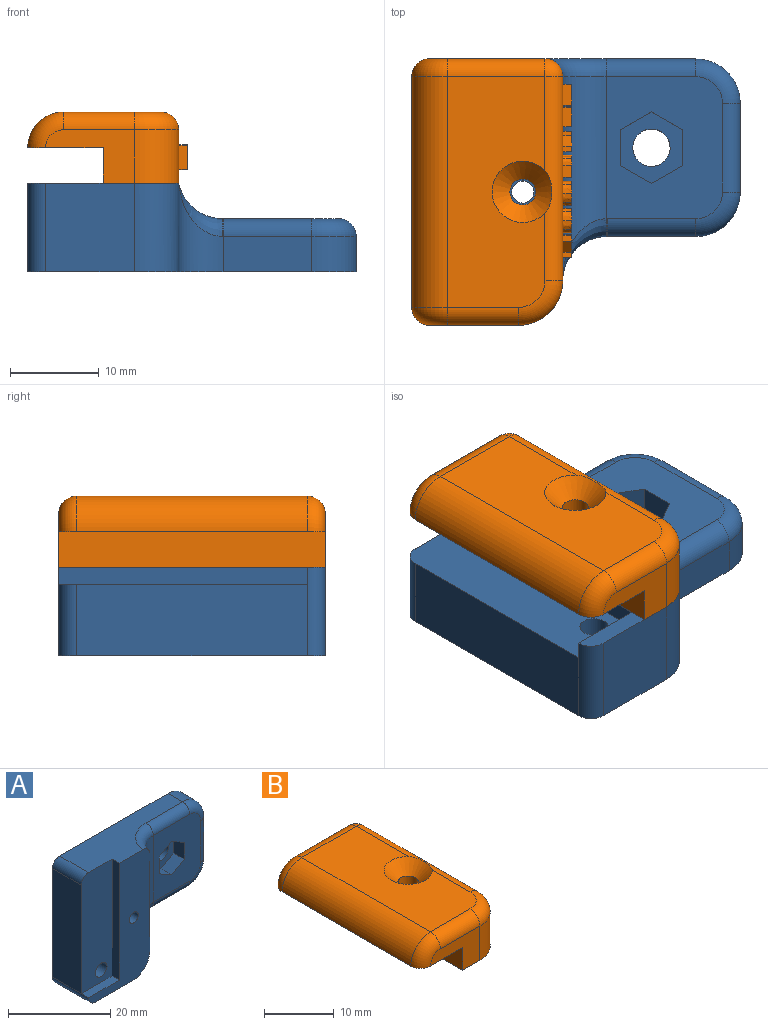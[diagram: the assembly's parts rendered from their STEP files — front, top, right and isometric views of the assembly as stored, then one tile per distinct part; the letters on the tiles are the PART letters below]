
ASSEMBLY  parts=2 mates=1
PART A: 43 faces, bbox 37.6x10.4x30.6 mm
  f0: cylinder r=1.6mm len=5.5mm, axis (0,-1,0), area 55.3mm2, adj f9,f32
  f1: cylinder r=2.1mm len=4.2mm, axis (0,-1,0), area 39.6mm2, adj f4,f25
  f2: plane 30x10mm, normal (0,0,1), area 194.9mm2, adj f3,f4,f8,f9,f18,f33,f34,f42
  f3: plane 30.15x17.15mm, normal (0,-1,0), area 260mm2, adj f2,f6,f7,f8,f13,f14,f15,f33
  f4: plane 37x30mm, normal (0,1,0), area 847.6mm2, adj f1,f2,f5,f6,f11,f12,f13,f14
  f5: plane 26x8mm, normal (-1,0,0), area 208mm2, adj f4,f9,f41,f42
  f6: plane 10x10mm, normal (0,0,-1), area 100mm2, adj f3,f4,f14,f41
  f7: plane 8.5x2mm, normal (0,0,1), area 17mm2, adj f3,f8,f9,f41
  f8: plane 28x2mm, normal (-1,0,0), area 56mm2, adj f2,f3,f7,f9
  f9: plane 28x8.5mm, normal (0,-1,0), area 229.1mm2, adj f0,f2,f5,f7,f8,f42
  f10: plane 16x13.1mm, normal (0,-1,0), area 163.3mm2, adj f15,f19,f20,f21,f22,f23,f24,f34
  f11: plane 10x4mm, normal (0,0,-1), area 40mm2, adj f4,f16,f17,f38
  f12: plane 10x4mm, normal (1,0,0), area 40mm2, adj f4,f17,f18,f36
  f13: cylinder r=1.25mm len=10mm, axis (0,-1,0), area 78.5mm2, adj f3,f4
  f14: cylinder r=5mm len=10mm, axis (0,1,0), area 78.5mm2, adj f3,f4,f6,f16,f40
  f15: cylinder r=5mm len=22.25mm, axis (0,0,1), area 124.1mm2, adj f3,f10,f33,f40
  f16: cylinder r=5mm len=9.82mm, axis (0,-1,0), area 49.9mm2, adj f4,f11,f14,f39,f40
  f17: cylinder r=5mm len=5mm, axis (0,-1,0), area 31.4mm2, adj f4,f11,f12,f37
  f18: cylinder r=5mm len=5mm, axis (0,1,0), area 31.4mm2, adj f2,f4,f12,f35
  f19: plane 3.5x3mm, normal (0.5,0,0.87), area 12.1mm2, adj f10,f20,f24,f25
  f20: plane 3.5x3mm, normal (-0.5,0,0.87), area 12.1mm2, adj f10,f19,f21,f25
  f21: plane 4.04x3mm, normal (-1,0,0), area 12.1mm2, adj f10,f20,f22,f25
  f22: plane 3.5x3mm, normal (-0.5,0,-0.87), area 12.1mm2, adj f10,f21,f23,f25
  f23: plane 3.5x3mm, normal (0.5,0,-0.87), area 12.1mm2, adj f10,f22,f24,f25
  f24: plane 4.04x3mm, normal (1,0,0), area 12.1mm2, adj f10,f19,f23,f25
  f25: plane 8.08x7mm, normal (0,-1,0), area 28.6mm2, adj f1,f19,f20,f21,f22,f23,f24
  f26: plane 3.46x2.5mm, normal (0,0,1), area 8.7mm2, adj f4,f27,f31,f32
  f27: plane 3x2.5mm, normal (0.87,0,0.5), area 8.7mm2, adj f4,f26,f28,f32
  f28: plane 3x2.5mm, normal (0.87,0,-0.5), area 8.7mm2, adj f4,f27,f29,f32
  f29: plane 3.46x2.5mm, normal (0,0,-1), area 8.7mm2, adj f4,f28,f30,f32
  f30: plane 3x2.5mm, normal (-0.87,0,-0.5), area 8.7mm2, adj f4,f29,f31,f32
  f31: plane 3x2.5mm, normal (-0.87,0,0.5), area 8.7mm2, adj f4,f26,f30,f32
  f32: plane 6.93x6mm, normal (0,1,0), area 23.1mm2, adj f0,f26,f27,f28,f29,f30,f31
  f33: torus R=7mm, axis (0,0,1), area 25.2mm2, adj f2,f3,f15,f34
  f34: cylinder r=2mm len=10.1mm, axis (-1,0,0), area 31.7mm2, adj f2,f10,f33,f35
  f35: torus R=3mm, axis (0,-1,0), area 21.1mm2, adj f10,f18,f34,f36
  f36: cylinder r=2mm len=10mm, axis (0,0,1), area 31.4mm2, adj f10,f12,f35,f37
  f37: torus R=3mm, axis (0,-1,0), area 21.1mm2, adj f10,f17,f36,f38
  f38: cylinder r=2mm len=10mm, axis (1,0,0), area 31.4mm2, adj f10,f11,f37,f39
  f39: torus R=7mm, axis (0,-1,0), area 0.3mm2, adj f10,f16,f38,f40
  f40: bspline ~7.5x6.16mm, area 17.8mm2, adj f3,f14,f15,f16,f39
  f41: cylinder r=2mm len=10mm, axis (0,-1,0), area 31.4mm2, adj f3,f4,f5,f6,f7
  f42: cylinder r=2mm len=8mm, axis (0,1,0), area 25.1mm2, adj f2,f4,f5,f9
PART B: 125 faces, bbox 18.3x30.4x8.3 mm
  f0: plane 23.02x6mm, normal (1,0,0), area 107.4mm2, adj f1,f9,f12,f14,f19,f20,f21,f22
  f1: plane 30.02x8.5mm, normal (0,0,-1), area 242.4mm2, adj f0,f2,f3,f4,f7,f9,f12
  f2: plane 13x6mm, normal (0,1,0), area 51.1mm2, adj f1,f6,f7,f10,f11,f12
  f3: plane 10x6mm, normal (0,-1,0), area 33.1mm2, adj f1,f6,f7,f9,f16,f17
  f4: cylinder r=1.45mm len=6mm, axis (0,0,-1), area 54.7mm2, adj f1,f18
  f5: plane 26.02x11mm, normal (0,0,1), area 250mm2, adj f8,f11,f14,f15,f16,f18
  f6: plane 30.02x8.5mm, normal (0,0,-1), area 253.5mm2, adj f2,f3,f7,f8,f10,f17
  f7: plane 30.02x4mm, normal (-1,0,0), area 120.1mm2, adj f1,f2,f3,f6
  f8: cylinder r=4mm len=26.02mm, axis (0,1,0), area 163.5mm2, adj f5,f6,f10,f17
  f9: cylinder r=5mm len=6mm, axis (0,0,1), area 47.1mm2, adj f0,f1,f3,f15
  f10: torus R=2mm, axis (0,1,0), area 16.2mm2, adj f2,f6,f8,f11
  f11: cylinder r=2mm len=11mm, axis (1,0,0), area 34.6mm2, adj f2,f5,f10,f13
  f12: cylinder r=2mm len=6mm, axis (0,0,-1), area 18.8mm2, adj f0,f1,f2,f13
  f13: sphere r=2mm, area 6.3mm2, adj f11,f12,f14
  f14: cylinder r=2mm len=23.02mm, axis (0,-1,0), area 69.6mm2, adj f0,f5,f13,f15,f18
  f15: torus R=3mm, axis (0,0,1), area 21.1mm2, adj f5,f9,f14,f16
  f16: cylinder r=2mm len=8mm, axis (-1,0,0), area 25.1mm2, adj f3,f5,f15,f17
  f17: torus R=2mm, axis (0,1,0), area 16.2mm2, adj f3,f6,f8,f16
  f18: cone r=1.45mm half-angle=45deg, axis (0,0,1), area 43mm2, adj f4,f5,f14
  f19: plane 1.25x1mm, normal (0,-0.79,-0.62), area 1.6mm2, adj f0,f20,f30,f31
  f20: plane 1x0.67mm, normal (0,0,-1), area 0.7mm2, adj f0,f19,f21,f31
  f21: plane 1.57x1.26mm, normal (0,0.78,0.63), area 2mm2, adj f0,f20,f22,f31
  f22: plane 1.16x1.15mm, normal (0,0.7,-0.71), area 1.6mm2, adj f0,f21,f23,f31
  f23: plane 1x0.66mm, normal (0,0,1), area 0.7mm2, adj f0,f22,f24,f31
  f24: plane 1.23x1.23mm, normal (0,-0.71,0.7), area 1.7mm2, adj f0,f23,f25,f31
  f25: plane 1.23x1mm, normal (0,1,0), area 1.2mm2, adj f0,f24,f26,f31
  f26: plane 1x0.57mm, normal (0,0,1), area 0.6mm2, adj f0,f25,f27,f31
  f27: plane 2.72x1mm, normal (0,-1,0), area 2.7mm2, adj f0,f26,f28,f31
  f28: plane 1x0.57mm, normal (0,0,-1), area 0.6mm2, adj f0,f27,f29,f31
  f29: plane 1x0.99mm, normal (0,1,0), area 1mm2, adj f0,f28,f30,f31
  f30: plane 1x0.34mm, normal (0,0.61,-0.79), area 0.4mm2, adj f0,f19,f29,f31
  f31: plane 2.72x2.55mm, normal (1,0,0), area 3.4mm2, adj f19,f20,f21,f22,f23,f24,f25,f26
  f32: extruded ~1x0.69mm, area 0.7mm2, adj f33,f48,f49,f50
  f33: extruded ~1x0.71mm, area 0.8mm2, adj f32,f34,f49,f50
  f34: extruded ~1x0.59mm, area 0.7mm2, adj f33,f35,f49,f50
  f35: extruded ~1x0.58mm, area 0.7mm2, adj f34,f36,f49,f50
  f36: extruded ~1x0.71mm, area 0.8mm2, adj f35,f37,f49,f50
  f37: extruded ~1x0.69mm, area 0.7mm2, adj f36,f38,f49,f50
  f38: extruded ~1x0.59mm, area 0.7mm2, adj f37,f48,f49,f50
  f39: extruded ~1x0.75mm, area 0.8mm2, adj f0,f40,f47,f49
  f40: extruded ~1.02x1mm, area 1.1mm2, adj f0,f39,f41,f49
  f41: extruded ~1.01x1mm, area 1.1mm2, adj f0,f40,f42,f49
  f42: extruded ~1.01x1mm, area 1.1mm2, adj f0,f41,f43,f49
  f43: extruded ~1.02x1mm, area 1.1mm2, adj f0,f42,f44,f49
  f44: extruded ~1.03x1mm, area 1.1mm2, adj f0,f43,f45,f49
  f45: extruded ~1x1mm, area 1.1mm2, adj f0,f44,f46,f49
  f46: extruded ~1x0.73mm, area 0.8mm2, adj f0,f45,f47,f49
  f47: extruded ~1x0.49mm, area 0.7mm2, adj f0,f39,f46,f49
  f48: extruded ~1x0.59mm, area 0.7mm2, adj f32,f38,f49,f50
  f49: plane 2.8x2.75mm, normal (1,0,0), area 3.8mm2, adj f32,f33,f34,f35,f36,f37,f38,f39
  f50: plane 1.9x1.59mm, normal (1,0,0), area 2.5mm2, adj f32,f33,f34,f35,f36,f37,f38,f48
  f51: extruded ~1x0.69mm, area 0.7mm2, adj f52,f67,f68,f69
  f52: extruded ~1x0.71mm, area 0.8mm2, adj f51,f53,f68,f69
  f53: extruded ~1x0.59mm, area 0.7mm2, adj f52,f54,f68,f69
  f54: extruded ~1x0.58mm, area 0.7mm2, adj f53,f55,f68,f69
  f55: extruded ~1x0.71mm, area 0.8mm2, adj f54,f56,f68,f69
  f56: extruded ~1x0.69mm, area 0.7mm2, adj f55,f57,f68,f69
  f57: extruded ~1x0.59mm, area 0.7mm2, adj f56,f67,f68,f69
  f58: extruded ~1x0.75mm, area 0.8mm2, adj f0,f59,f66,f68
  f59: extruded ~1.02x1mm, area 1.1mm2, adj f0,f58,f60,f68
  f60: extruded ~1.01x1mm, area 1.1mm2, adj f0,f59,f61,f68
  f61: extruded ~1.01x1mm, area 1.1mm2, adj f0,f60,f62,f68
  f62: extruded ~1.02x1mm, area 1.1mm2, adj f0,f61,f63,f68
  f63: extruded ~1.03x1mm, area 1.1mm2, adj f0,f62,f64,f68
  f64: extruded ~1x1mm, area 1.1mm2, adj f0,f63,f65,f68
  f65: extruded ~1x0.73mm, area 0.8mm2, adj f0,f64,f66,f68
  f66: extruded ~1x0.49mm, area 0.7mm2, adj f0,f58,f65,f68
  f67: extruded ~1x0.59mm, area 0.7mm2, adj f51,f57,f68,f69
  f68: plane 2.8x2.75mm, normal (1,0,0), area 3.8mm2, adj f51,f52,f53,f54,f55,f56,f57,f58
  f69: plane 1.9x1.59mm, normal (1,0,0), area 2.5mm2, adj f51,f52,f53,f54,f55,f56,f57,f67
  f70: extruded ~1x0.5mm, area 0.7mm2, adj f71,f87,f88,f89
  f71: extruded ~1x0.3mm, area 0.3mm2, adj f70,f72,f88,f89
  f72: extruded ~1x0.36mm, area 0.4mm2, adj f71,f73,f88,f89
  f73: plane 1x0.75mm, normal (0,0,1), area 0.7mm2, adj f72,f74,f88,f89
  f74: plane 1x0.8mm, normal (0,1,0), area 0.8mm2, adj f73,f87,f88,f89
  f75: plane 1.03x1mm, normal (0,-0.85,-0.52), area 1.2mm2, adj f0,f76,f86,f88
  f76: plane 1x0.64mm, normal (0,0,-1), area 0.6mm2, adj f0,f75,f77,f88
  f77: plane 1.14x1mm, normal (0,0.84,0.54), area 1.4mm2, adj f0,f76,f78,f88
  f78: extruded ~1x0.44mm, area 0.5mm2, adj f0,f77,f79,f88
  f79: extruded ~1x0.49mm, area 0.5mm2, adj f0,f78,f80,f88
  f80: extruded ~1x0.6mm, area 0.7mm2, adj f0,f79,f81,f88
  f81: extruded ~1x0.75mm, area 0.8mm2, adj f0,f80,f82,f88
  f82: plane 1.36x1mm, normal (0,0,1), area 1.4mm2, adj f0,f81,f83,f88
  f83: plane 2.72x1mm, normal (0,-1,0), area 2.7mm2, adj f0,f82,f84,f88
  f84: plane 1x0.57mm, normal (0,0,-1), area 0.6mm2, adj f0,f83,f85,f88
  f85: plane 1.03x1mm, normal (0,1,0), area 1mm2, adj f0,f84,f86,f88
  f86: plane 1x0.67mm, normal (0,0,-1), area 0.7mm2, adj f0,f75,f85,f88
  f87: plane 1x0.73mm, normal (0,0,-1), area 0.7mm2, adj f70,f74,f88,f89
  f88: plane 2.72x2.51mm, normal (1,0,0), area 4mm2, adj f70,f71,f72,f73,f74,f75,f76,f77
  f89: plane 1.23x0.8mm, normal (1,0,0), area 0.9mm2, adj f70,f71,f72,f73,f74,f87
  f90: plane 2.09x1.19mm, normal (0,-0.87,-0.49), area 2.4mm2, adj f0,f91,f101,f102
  f91: plane 1x0.67mm, normal (0,0,-1), area 0.7mm2, adj f0,f90,f92,f102
  f92: plane 2.72x1mm, normal (0,1,0), area 2.7mm2, adj f0,f91,f93,f102
  f93: plane 1x0.51mm, normal (0,0,1), area 0.5mm2, adj f0,f92,f94,f102
  f94: plane 1.58x1mm, normal (0,-1,0), area 1.6mm2, adj f0,f93,f95,f102
  f95: extruded ~1x0.53mm, area 0.5mm2, adj f0,f94,f96,f102
  f96: plane 2.11x1.2mm, normal (0,0.87,0.49), area 2.4mm2, adj f0,f95,f97,f102
  f97: plane 1x0.65mm, normal (0,0,1), area 0.7mm2, adj f0,f96,f98,f102
  f98: plane 2.72x1mm, normal (0,-1,0), area 2.7mm2, adj f0,f97,f99,f102
  f99: plane 1x0.51mm, normal (0,0,-1), area 0.5mm2, adj f0,f98,f100,f102
  f100: plane 1.6x1mm, normal (0,1,0), area 1.6mm2, adj f0,f99,f101,f102
  f101: extruded ~1x0.49mm, area 0.5mm2, adj f0,f90,f100,f102
  f102: plane 2.72x2.32mm, normal (1,0,0), area 3.9mm2, adj f90,f91,f92,f93,f94,f95,f96,f97
  f103: plane 2.72x1mm, normal (0,-1,0), area 2.7mm2, adj f0,f104,f114,f115
  f104: plane 2.22x1mm, normal (0,0,-1), area 2.2mm2, adj f0,f103,f105,f115
  f105: plane 1x0.44mm, normal (0,1,0), area 0.4mm2, adj f0,f104,f106,f115
  f106: plane 1.65x1mm, normal (0,0,1), area 1.6mm2, adj f0,f105,f107,f115
  f107: plane 1x0.72mm, normal (0,1,0), area 0.7mm2, adj f0,f106,f108,f115
  f108: plane 1.45x1mm, normal (0,0,-1), area 1.5mm2, adj f0,f107,f109,f115
  f109: plane 1x0.44mm, normal (0,1,0), area 0.4mm2, adj f0,f108,f110,f115
  f110: plane 1.45x1mm, normal (0,0,1), area 1.5mm2, adj f0,f109,f111,f115
  f111: plane 1x0.68mm, normal (0,1,0), area 0.7mm2, adj f0,f110,f112,f115
  f112: plane 1.57x1mm, normal (0,0,-1), area 1.6mm2, adj f0,f111,f113,f115
  f113: plane 1x0.44mm, normal (0,1,0), area 0.4mm2, adj f0,f112,f114,f115
  f114: plane 2.14x1mm, normal (0,0,1), area 2.1mm2, adj f0,f103,f113,f115
  f115: plane 2.72x2.22mm, normal (1,0,0), area 3.6mm2, adj f103,f104,f105,f106,f107,f108,f109,f110
  f116: plane 2.28x1mm, normal (0,1,0), area 2.3mm2, adj f0,f117,f123,f124
  f117: plane 1x0.88mm, normal (0,0,-1), area 0.9mm2, adj f0,f116,f118,f124
  f118: plane 1x0.44mm, normal (0,1,0), area 0.4mm2, adj f0,f117,f119,f124
  f119: plane 2.33x1mm, normal (0,0,1), area 2.3mm2, adj f0,f118,f120,f124
  f120: plane 1x0.44mm, normal (0,-1,0), area 0.4mm2, adj f0,f119,f121,f124
  f121: plane 1x0.88mm, normal (0,0,-1), area 0.9mm2, adj f0,f120,f122,f124
  f122: plane 2.28x1mm, normal (0,-1,0), area 2.3mm2, adj f0,f121,f123,f124
  f123: plane 1x0.57mm, normal (0,0,-1), area 0.6mm2, adj f0,f116,f122,f124
  f124: plane 2.72x2.33mm, normal (1,0,0), area 2.3mm2, adj f116,f117,f118,f119,f120,f121,f122,f123
PLACE A rot(axis=(-1,0,0),90deg) t=(-51.53,-29.38,43.62)mm
PLACE B t=(-26.81,-12,48.62)mm
MATE fastened A.f13 <-> B.f4  axis (0,0,1) through (-47.53,-14.38,48.62)mm
